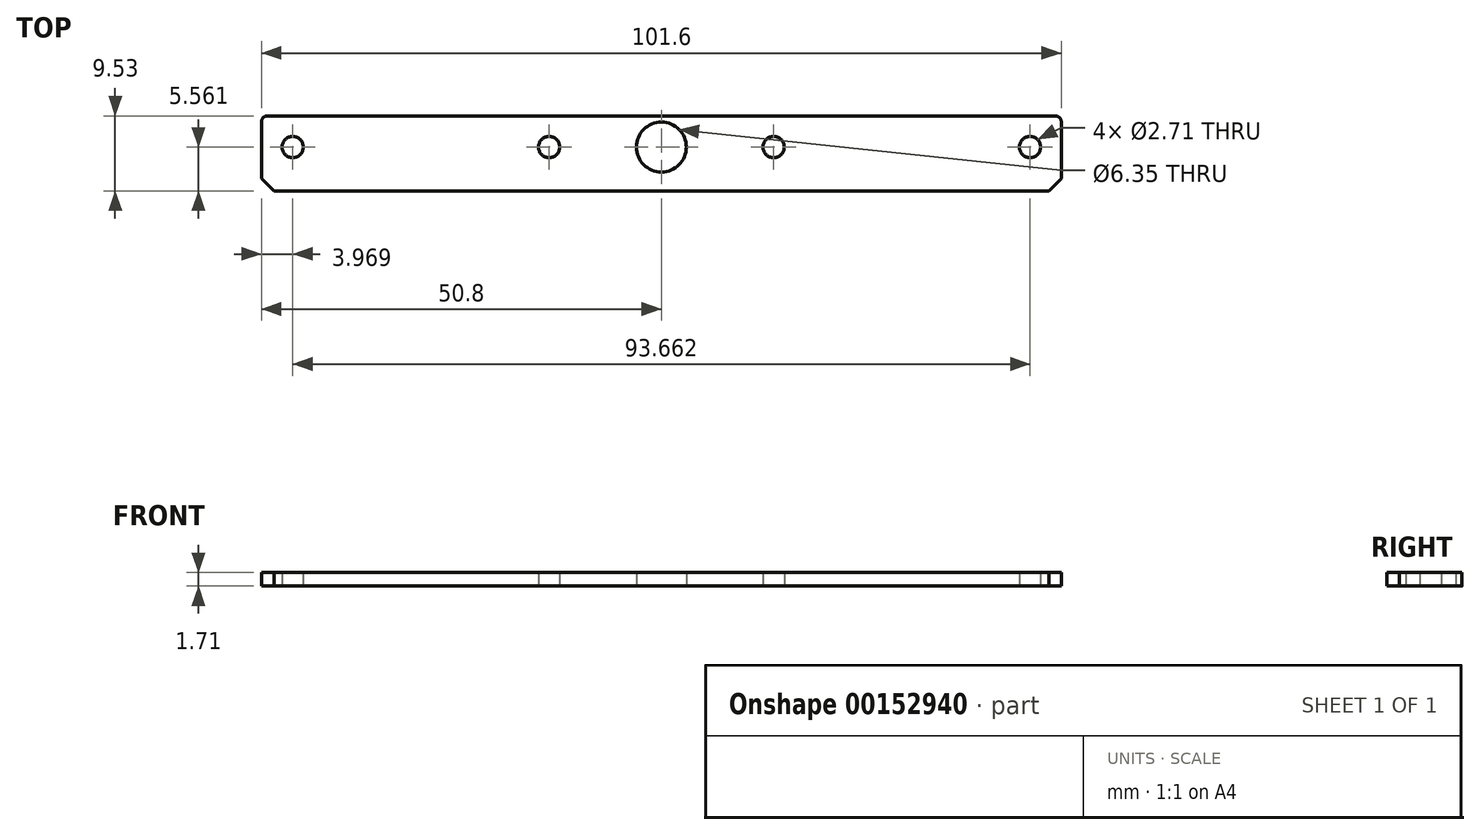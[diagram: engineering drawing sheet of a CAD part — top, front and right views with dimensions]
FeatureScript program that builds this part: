
annotation { "Feature Type Name" : "Feature", "Feature Type Description" : "" }
export const myFeature = defineFeature(function(context is Context, id is Id, definition is map)
    precondition{}
    {
        {
            var Q0;
            Q0=qCreatedBy(makeId("Top.planeOp"),FACE);
            var sketch = newSketch(context, id + "F0", { "sketchPlane" : qUnion([Q0])});
            skLineSegment(sketch, "E0.bottom", {"start": v(0, 0) * mm, "end": v(-101.6, 0) * mm});
            skLineSegment(sketch, "E0.top", {"start": v(0, -9.53) * mm, "end": v(-101.6, -9.53) * mm});
            skLineSegment(sketch, "E0.left", {"start": v(0, 0) * mm, "end": v(0, -9.53) * mm});
            skLineSegment(sketch, "E0.right", {"start": v(-101.6, 0) * mm, "end": v(-101.6, -9.53) * mm});
            skLineSegment(sketch, "E1", {"start": v(-50.8, 0) * mm, "end": v(-50.8, -3.97) * mm, "construction": true});
            skLineSegment(sketch, "E2", {"start": v(-65.06, -3.97) * mm, "end": v(-36.54, -3.97) * mm, "construction": true});
            skLineSegment(sketch, "E3", {"start": v(0, -3.97) * mm, "end": v(-3.97, -3.97) * mm, "construction": true});
            skLineSegment(sketch, "E4", {"start": v(-101.6, -3.97) * mm, "end": v(-97.63, -3.97) * mm, "construction": true});
            skCircle(sketch, "E5", {"center": v(-97.63, -3.97) * mm, "radius": 1.35 * mm});
            skCircle(sketch, "E6", {"center": v(-65.06, -3.97) * mm, "radius": 1.35 * mm});
            skCircle(sketch, "E7", {"center": v(-36.54, -3.97) * mm, "radius": 1.35 * mm});
            skCircle(sketch, "E8", {"center": v(-3.97, -3.97) * mm, "radius": 1.35 * mm});
            skCircle(sketch, "E9", {"center": v(-50.8, -3.97) * mm, "radius": 3.18 * mm});
            skSolve(sketch);
        }
        {
            var Q0;
            Q0 = qSketchRegion(id + "F0", true);
            extrude(context, id + "F1", {"entities" : qUnion([Q0]), "depth" : 1.7 * mm});
        }
        {
            var Q0;
            Q0=makeQuery(id+"F1.opExtrude","SWEPT_EDGE",EDGE,{"disambiguationData":[OSD([sQuery(id+"F0.wireOp",EDGE,"E0.bottom"),sQuery(id+"F0.wireOp",EDGE,"E0.right")])]});
            var Q1;
            Q1=makeQuery(id+"F1.opExtrude","SWEPT_EDGE",EDGE,{"disambiguationData":[OSD([sQuery(id+"F0.wireOp",EDGE,"E0.bottom"),sQuery(id+"F0.wireOp",EDGE,"E0.left")])]});
            fillet(context, id + "F2", {"entities" : qUnion([Q0, Q1]), "radius" : 0.76 * mm, "tangentPropagation" : true, "allowEdgeOverflow" : false});
        }
        {
            var Q0;
            Q0=makeQuery(id+"F1.opExtrude","SWEPT_EDGE",EDGE,{"disambiguationData":[OSD([sQuery(id+"F0.wireOp",EDGE,"E0.top"),sQuery(id+"F0.wireOp",EDGE,"E0.left")])]});
            var Q1;
            Q1=makeQuery(id+"F1.opExtrude","SWEPT_EDGE",EDGE,{"disambiguationData":[OSD([sQuery(id+"F0.wireOp",EDGE,"E0.top"),sQuery(id+"F0.wireOp",EDGE,"E0.right")])]});
            chamfer(context, id + "F3", {"entities" : qUnion([Q0, Q1]), "width" : 1.59 * mm, "tangentPropagation" : true});
        }
    });
